# Revit family: 63_UN_LF_SM_Code BB3
name_source: partatom
category: Lighting Fixtures
units: mm (PartAtom-declared; Revit-internal decimal feet)

## family parameters
Always vertical = Yes
Cut with Voids When Loaded = Yes
Light Source = No
OmniClass Number = 23.80.70.11.14
OmniClass Title = General Luminaries, Directional
Part Type = Normal
Room Calculation Point = Yes
Round Connector Dimension = Use Diameter
Shared = No
Work Plane-Based = No

## types (2) — shared parameters
Apparent Load = 4 VA
Assembly Code = 63.0
Housing_Material = Plastic, Opaque Black
IfcExportAs = IfcLightFixtureType
IfcExportType = USERDEFINED
Lamp = LED
Light Source = BB3 Geometry
Luminous Flux (lm) = 578 lm
Manufacturer = Light International
Model = BB3
Type Comments = BB3
URL = https://lightinternational.nl
Voltage = 230 V
Wattage Comments = 4.3W

## per-type parameters (varying)
| type | Lightsource_tilt |
| BB3 - Wall mounted | 90.00° |
| BB3 - Ceiling mounted | 180.00° |

## geometry (parser evidence)
native form markers: Sweep x16
no freeform markers — native parametric forms only
